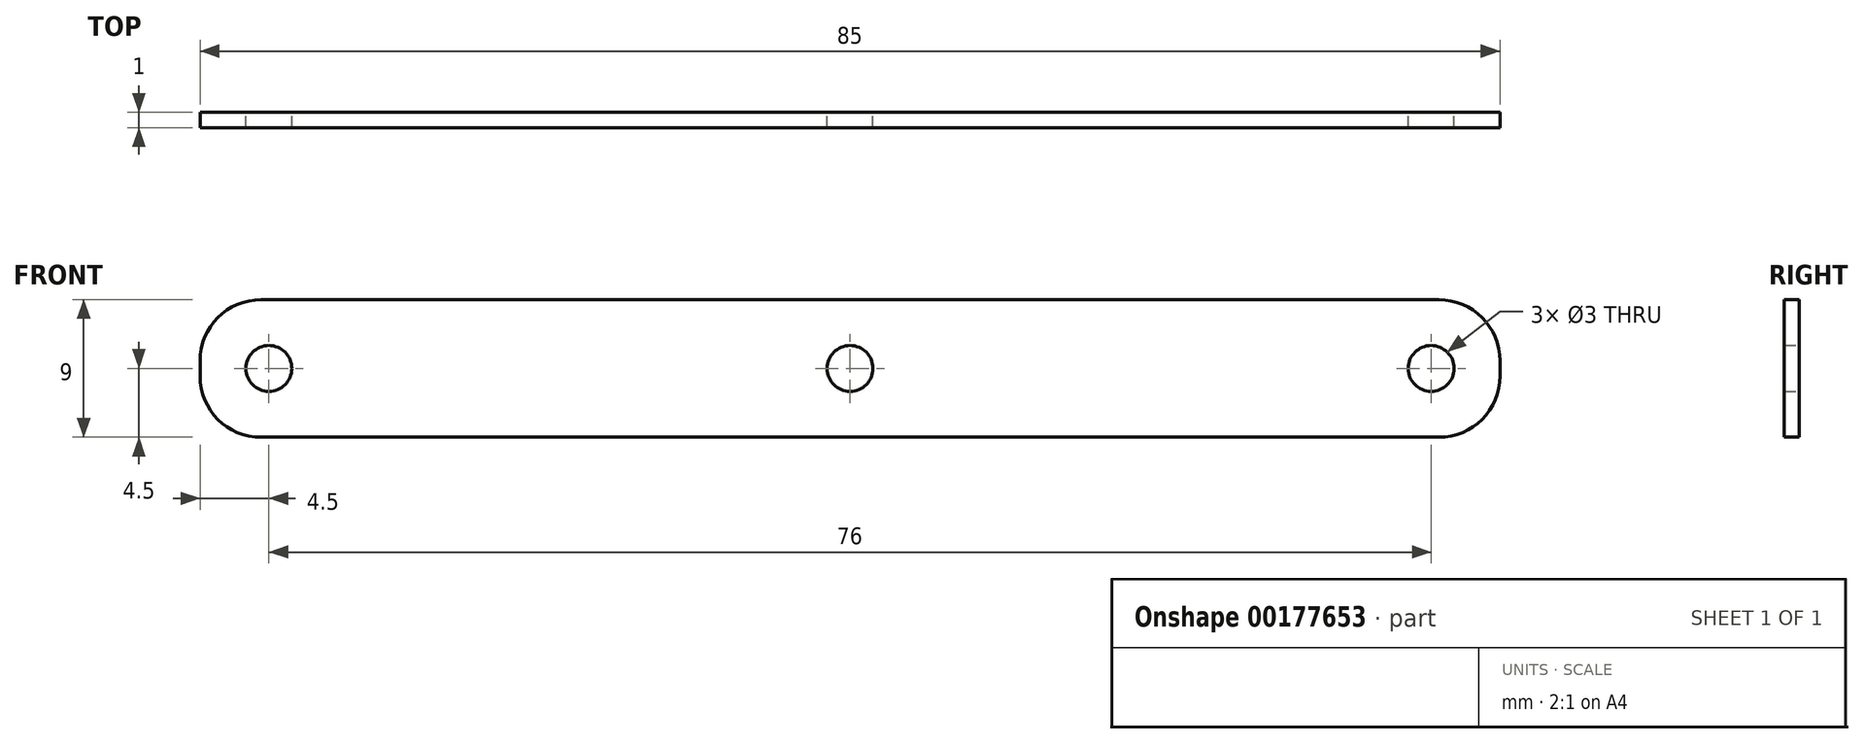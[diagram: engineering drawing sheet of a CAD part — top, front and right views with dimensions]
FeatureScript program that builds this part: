
annotation { "Feature Type Name" : "Feature", "Feature Type Description" : "" }
export const myFeature = defineFeature(function(context is Context, id is Id, definition is map)
    precondition{}
    {
        {
            var Q0;
            Q0=qCreatedBy(makeId("Front.planeOp"),FACE);
            var sketch = newSketch(context, id + "F0", { "sketchPlane" : qUnion([Q0])});
            skLineSegment(sketch, "E0.bottom", {"start": v(42.5, 4.5) * mm, "end": v(-42.5, 4.5) * mm});
            skLineSegment(sketch, "E0.top", {"start": v(42.5, -4.5) * mm, "end": v(-42.5, -4.5) * mm});
            skLineSegment(sketch, "E0.left", {"start": v(42.5, 4.5) * mm, "end": v(42.5, -4.5) * mm});
            skLineSegment(sketch, "E0.right", {"start": v(-42.5, 4.5) * mm, "end": v(-42.5, -4.5) * mm});
            skPoint(sketch, "E0.middle", {"position": v(0, 0) * mm});
            skCircle(sketch, "E1", {"center": v(0, 0) * mm, "radius": 1.5 * mm});
            skCircle(sketch, "E2", {"center": v(38, 0) * mm, "radius": 1.5 * mm});
            skCircle(sketch, "E3", {"center": v(-38, 0) * mm, "radius": 1.5 * mm});
            skSolve(sketch);
        }
        {
            var Q0;
            Q0 = qSketchRegion(id + "F0", true);
            extrude(context, id + "F1", {"entities" : qUnion([Q0]), "depth" : 1 * mm});
        }
        {
            var Q0;
            Q0=makeQuery(id+"F1.opExtrude","SWEPT_EDGE",EDGE,{"disambiguationData":[OSD([sQuery(id+"F0.wireOp",EDGE,"E0.bottom"),sQuery(id+"F0.wireOp",EDGE,"E0.right")])]});
            var Q1;
            Q1=makeQuery(id+"F1.opExtrude","SWEPT_EDGE",EDGE,{"disambiguationData":[OSD([sQuery(id+"F0.wireOp",EDGE,"E0.top"),sQuery(id+"F0.wireOp",EDGE,"E0.right")])]});
            var Q2;
            Q2=makeQuery(id+"F1.opExtrude","SWEPT_EDGE",EDGE,{"disambiguationData":[OSD([sQuery(id+"F0.wireOp",EDGE,"E0.top"),sQuery(id+"F0.wireOp",EDGE,"E0.left")])]});
            var Q3;
            Q3=makeQuery(id+"F1.opExtrude","SWEPT_EDGE",EDGE,{"disambiguationData":[OSD([sQuery(id+"F0.wireOp",EDGE,"E0.bottom"),sQuery(id+"F0.wireOp",EDGE,"E0.left")])]});
            fillet(context, id + "F2", {"entities" : qUnion([Q0, Q1, Q2, Q3]), "radius" : 4 * mm, "tangentPropagation" : true, "allowEdgeOverflow" : false});
        }
    });
